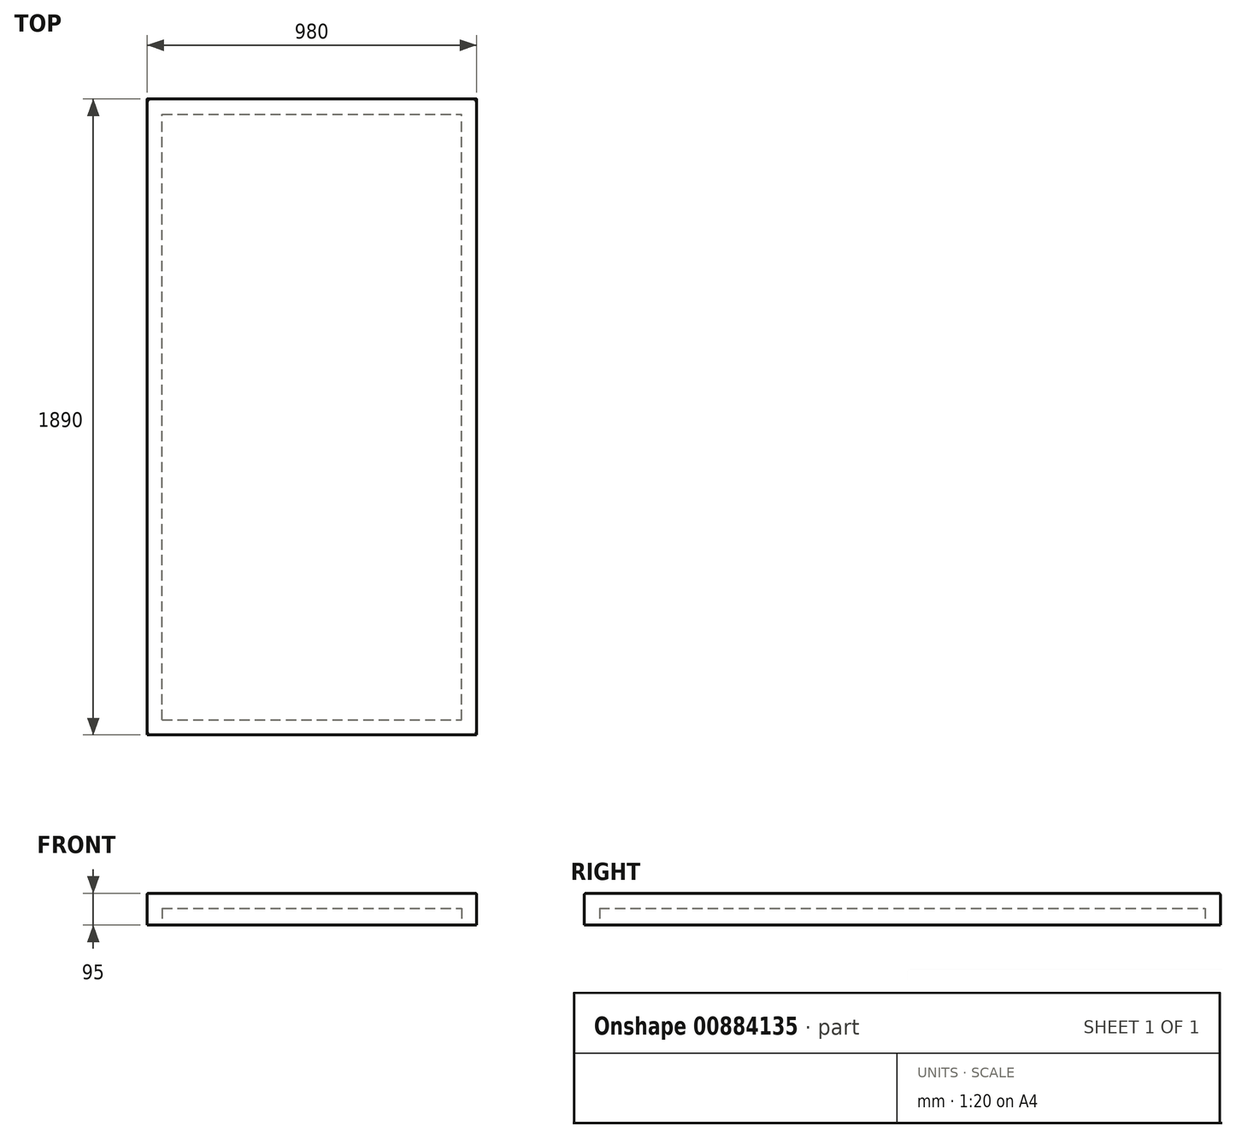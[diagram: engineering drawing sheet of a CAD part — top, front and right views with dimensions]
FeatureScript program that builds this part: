
annotation { "Feature Type Name" : "Feature", "Feature Type Description" : "" }
export const myFeature = defineFeature(function(context is Context, id is Id, definition is map)
    precondition{}
    {
        {
            var Q0;
            Q0=qCreatedBy(makeId("Top.planeOp"),FACE);
            var sketch = newSketch(context, id + "F0", { "sketchPlane" : qUnion([Q0])});
            skLineSegment(sketch, "E0.bottom", {"start": v(-490, 945) * mm, "end": v(490, 945) * mm});
            skLineSegment(sketch, "E0.top", {"start": v(-490, -945) * mm, "end": v(490, -945) * mm});
            skLineSegment(sketch, "E0.left", {"start": v(-490, 945) * mm, "end": v(-490, -945) * mm});
            skLineSegment(sketch, "E0.right", {"start": v(490, 945) * mm, "end": v(490, -945) * mm});
            skPoint(sketch, "E0.middle", {"position": v(0, 0) * mm});
            skSolve(sketch);
        }
        {
            var Q0;
            Q0 = qSketchRegion(id + "F0", true);
            extrude(context, id + "F1", {"entities" : qUnion([Q0]), "depth" : 70 * mm, "offsetDistance" : 25 * mm});
        }
        {
            var Q0;
            Q0=makeQuery(id+"F1.opExtrude","CAP_EDGE",EDGE,{"disambiguationData":[OSD([sQuery(id+"F0.wireOp",EDGE,"E0.bottom")])],"isStart":false});
            var Q1;
            Q1=makeQuery(id+"F1.opExtrude","CAP_EDGE",EDGE,{"disambiguationData":[OSD([sQuery(id+"F0.wireOp",EDGE,"E0.left")])],"isStart":false});
            var Q2;
            Q2=makeQuery(id+"F1.opExtrude","CAP_EDGE",EDGE,{"disambiguationData":[OSD([sQuery(id+"F0.wireOp",EDGE,"E0.top")])],"isStart":false});
            var Q3;
            Q3=makeQuery(id+"F1.opExtrude","CAP_EDGE",EDGE,{"disambiguationData":[OSD([sQuery(id+"F0.wireOp",EDGE,"E0.right")])],"isStart":false});
            fillet(context, id + "F2", {"entities" : qUnion([Q0, Q1, Q2, Q3]), "radius" : 5 * mm, "tangentPropagation" : true, "allowEdgeOverflow" : false});
        }
        {
            var Q0;
            Q0=makeQuery(id+"F1.opExtrude","CAP_FACE",FACE,{"disambiguationData":[OSD([sQuery(id+"F0.wireOp",EDGE,"E0.bottom"),sQuery(id+"F0.wireOp",EDGE,"E0.top"),sQuery(id+"F0.wireOp",EDGE,"E0.left"),sQuery(id+"F0.wireOp",EDGE,"E0.right")])],"isStart":true});
            var sketch = newSketch(context, id + "F3", { "sketchPlane" : qUnion([Q0])});
            skSolve(sketch);
        }
        {
            var Q0;
            Q0 = qSketchRegion(id + "F3", true);
            var Q1;
            Q1=makeQuery(id+"F3.imprint","IMPRINT",FACE,{"disambiguationData":[TD([[makeQuery(id+"F3.imprint","IMPRINT",EDGE,{"derivedFrom":makeQuery(id+"F1.opExtrude","CAP_EDGE",EDGE,{"disambiguationData":[OSD([sQuery(id+"F0.wireOp",EDGE,"E0.bottom")])],"isStart":true})}),1.0]])]});
            var Q2;
            Q2=makeQuery(id+"F1.opExtrude","CAP_FACE",FACE,{"disambiguationData":[OSD([sQuery(id+"F0.wireOp",EDGE,"E0.bottom"),sQuery(id+"F0.wireOp",EDGE,"E0.top"),sQuery(id+"F0.wireOp",EDGE,"E0.left"),sQuery(id+"F0.wireOp",EDGE,"E0.right")])],"isStart":true});
            var Q3;
            Q3=makeQuery(id+"F1.opExtrude","CAP_FACE",FACE,{"disambiguationData":[OSD([sQuery(id+"F0.wireOp",EDGE,"E0.bottom"),sQuery(id+"F0.wireOp",EDGE,"E0.top"),sQuery(id+"F0.wireOp",EDGE,"E0.left"),sQuery(id+"F0.wireOp",EDGE,"E0.right")])],"isStart":false});
            extrude(context, id + "F4", {"entities" : qUnion([Q0, Q1, Q2, Q3]), "operationType" : NewBodyOperationType.ADD, "depth" : 25 * mm, "offsetDistance" : 25 * mm});
        }
        {
            var Q0;
            {var subQ0=sQuery(id+"F0.wireOp",EDGE,"E0.right");var subQ1=sQuery(id+"F0.wireOp",EDGE,"E0.left");var subQ2=sQuery(id+"F0.wireOp",EDGE,"E0.top");var subQ3=sQuery(id+"F0.wireOp",EDGE,"E0.bottom");Q0=makeQuery(id+"F4.opExtrude","CAP_FACE",FACE,{"disambiguationData":[OSD([subQ3,subQ2,subQ1,subQ0]),TDD([makeQuery(id+"F1.opExtrude","CAP_FACE",FACE,{"disambiguationData":[OSD([subQ3,subQ2,subQ1,subQ0])],"isStart":true})])],"isStart":false});}
            var sketch = newSketch(context, id + "F5", { "sketchPlane" : qUnion([Q0])});
            skLineSegment(sketch, "E1.bottom", {"start": v(-445, 900) * mm, "end": v(445, 900) * mm});
            skLineSegment(sketch, "E1.top", {"start": v(-445, -900) * mm, "end": v(445, -900) * mm});
            skLineSegment(sketch, "E1.left", {"start": v(-445, 900) * mm, "end": v(-445, -900) * mm});
            skLineSegment(sketch, "E1.right", {"start": v(445, 900) * mm, "end": v(445, -900) * mm});
            skPoint(sketch, "E1.middle", {"position": v(0, 0) * mm});
            skSolve(sketch);
        }
        {
            var Q0;
            Q0=makeQuery(id+"F5.imprint","IMPRINT",FACE,{"disambiguationData":[TD([[makeQuery(id+"F5.imprint","IMPRINT",EDGE,{"derivedFrom":sQuery(id+"F5.wireOp",EDGE,"E1.bottom")}),-1.0]])]});
            extrude(context, id + "F6", {"entities" : qUnion([Q0]), "operationType" : NewBodyOperationType.REMOVE, "oppositeDirection" : true, "depth" : 50 * mm, "offsetDistance" : 25 * mm});
        }
    });
